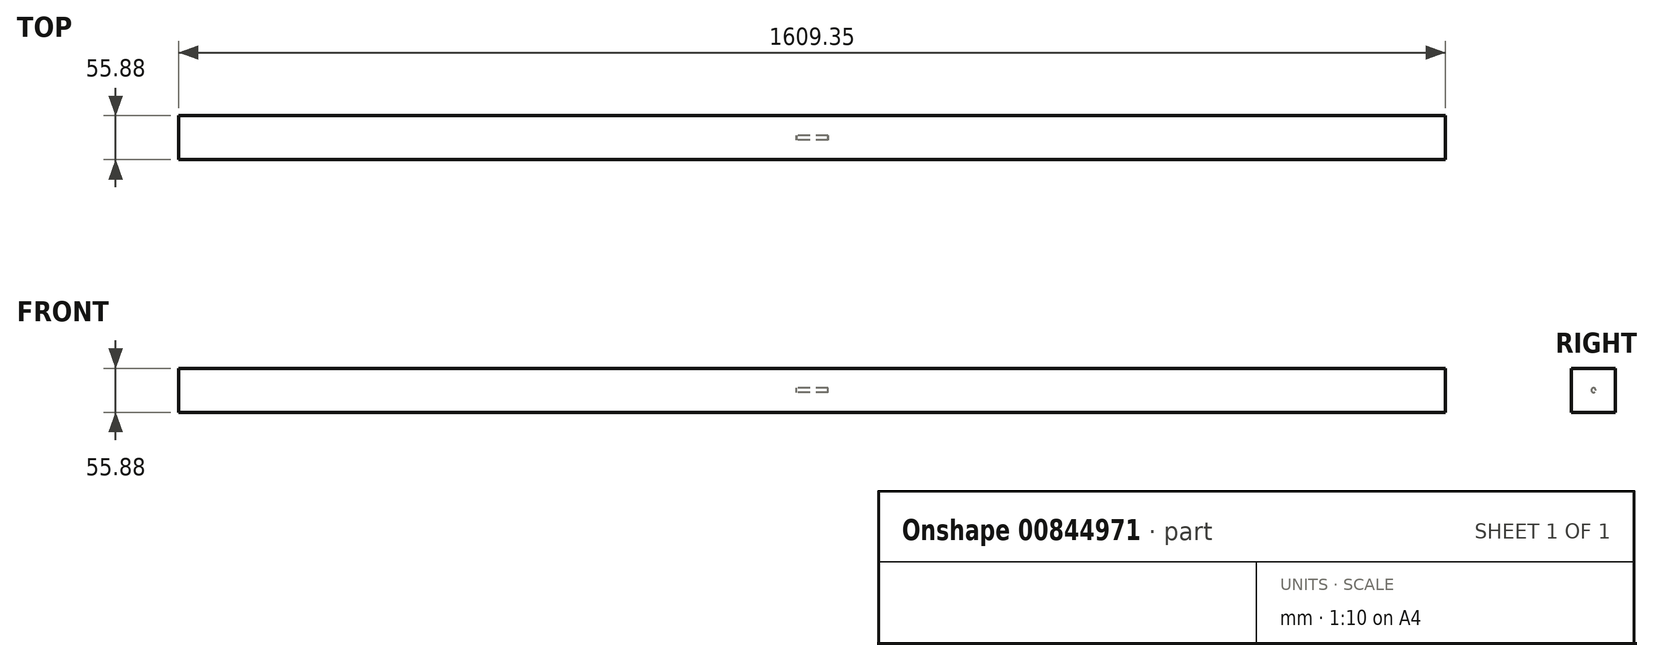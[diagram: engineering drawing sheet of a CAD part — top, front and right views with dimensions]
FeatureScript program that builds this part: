
annotation { "Feature Type Name" : "Feature", "Feature Type Description" : "" }
export const myFeature = defineFeature(function(context is Context, id is Id, definition is map)
    precondition{}
    {
        {
            var Q0;
            Q0=qCreatedBy(makeId("Right.planeOp"),FACE);
            var sketch = newSketch(context, id + "F0", { "sketchPlane" : qUnion([Q0])});
            skCircle(sketch, "E0", {"center": v(0, 0) * mm, "radius": 2.8 * mm});
            skSolve(sketch);
        }
        {
            var Q0;
            Q0=makeQuery(id+"F0.imprint","IMPRINT",FACE,{"disambiguationData":[TD([[makeQuery(id+"F0.imprint","IMPRINT",EDGE,{"derivedFrom":sQuery(id+"F0.wireOp",EDGE,"E0")}),1.0]])]});
            extrude(context, id + "F1", {"entities" : qUnion([Q0]), "depth" : 40.23 * mm, "offsetDistance" : 25.4 * mm});
        }
        {
            var Q0;
            Q0=qCreatedBy(makeId("Right.planeOp"),FACE);
            cPlane(context, id + "F2", {"entities" : qUnion([Q0]), "cplaneType" : CPlaneType.OFFSET, "offset" : 824.8 * mm, "width" : 152.4 * mm, "height" : 152.4 * mm});
        }
        {
            var Q0;
            Q0=qCreatedBy(id+"F2.planeOp",FACE);
            var sketch = newSketch(context, id + "F3", { "sketchPlane" : qUnion([Q0])});
            skLineSegment(sketch, "E1.bottom", {"start": v(27.94, -27.94) * mm, "end": v(-27.94, -27.94) * mm});
            skLineSegment(sketch, "E1.top", {"start": v(27.94, 27.94) * mm, "end": v(-27.94, 27.94) * mm});
            skLineSegment(sketch, "E1.left", {"start": v(27.94, -27.94) * mm, "end": v(27.94, 27.94) * mm});
            skLineSegment(sketch, "E1.right", {"start": v(-27.94, -27.94) * mm, "end": v(-27.94, 27.94) * mm});
            skPoint(sketch, "E1.middle", {"position": v(0, 0) * mm});
            skSolve(sketch);
        }
        {
            var Q0;
            Q0 = qSketchRegion(id + "F3", true);
            extrude(context, id + "F4", {"entities" : qUnion([Q0]), "oppositeDirection" : true, "depth" : 1609.34 * mm, "offsetDistance" : 25.4 * mm});
        }
    });
